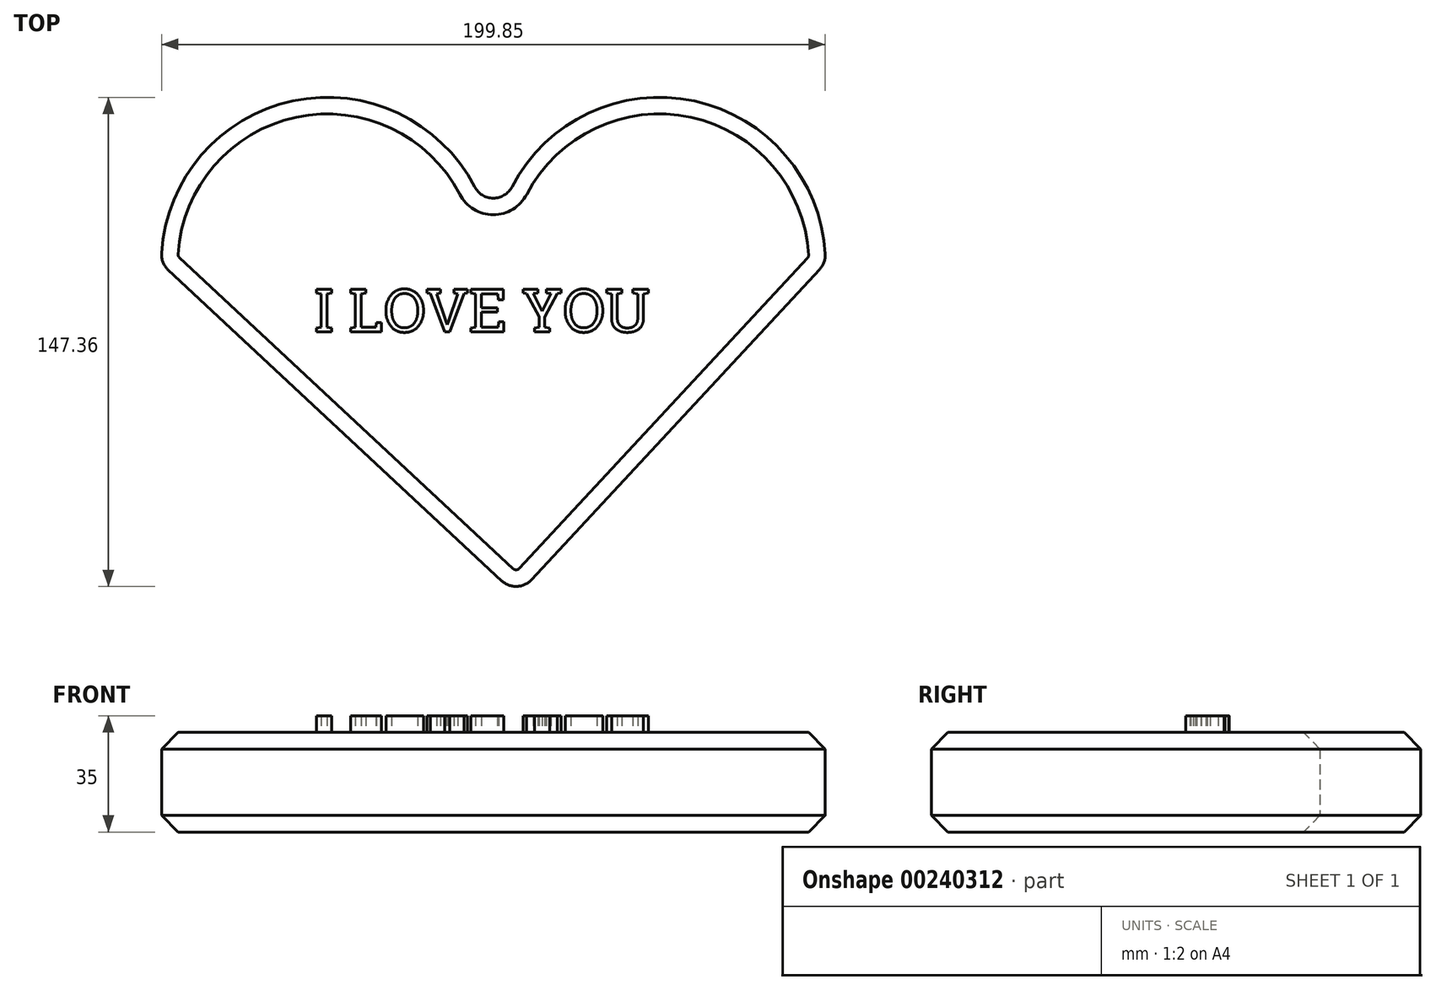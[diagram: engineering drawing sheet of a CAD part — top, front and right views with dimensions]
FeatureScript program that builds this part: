
annotation { "Feature Type Name" : "Feature", "Feature Type Description" : "" }
export const myFeature = defineFeature(function(context is Context, id is Id, definition is map)
    precondition{}
    {
        {
            var Q0;
            Q0=qCreatedBy(makeId("Top.planeOp"),FACE);
            var sketch = newSketch(context, id + "F0", { "sketchPlane" : qUnion([Q0])});
            skLineSegment(sketch, "E0.left", {"start": v(-50, 0) * mm, "end": v(-50, 3.36) * mm, "construction": true});
            skPoint(sketch, "E0.middle", {"position": v(0, 0) * mm});
            skArc(sketch, "E1", {"start": v(-50, 0) * mm, "mid": v(-48.26, 0.03) * mm, "end": v(-46.52, 0.12) * mm});
            skArc(sketch, "E2", {"start": v(50, 0) * mm, "mid": v(51.87, 0.03) * mm, "end": v(53.73, 0.14) * mm});
            skLineSegment(sketch, "E3", {"start": v(2.55, -45.66) * mm, "end": v(-97.9, 48.04) * mm});
            skLineSegment(sketch, "E4", {"start": v(11.54, -45.33) * mm, "end": v(98.24, 48.1) * mm});
            skArc(sketch, "E5.trimOffspring", {"start": v(-5.63, 73.06) * mm, "mid": v(-60.37, 98.91) * mm, "end": v(-99.9, 53.07) * mm});
            skArc(sketch, "E6.trimOffspring", {"start": v(99.92, 52.77) * mm, "mid": v(60.52, 98.88) * mm, "end": v(5.63, 73.06) * mm});
            skPoint(sketch, "E7.orphan", {"position": v(-50, -50) * mm});
            skPoint(sketch, "E8.orphan", {"position": v(50, -50) * mm});
            skPoint(sketch, "E9.visualSharp", {"position": v(0, 50) * mm});
            skArc(sketch, "E9.filletArc", {"start": v(-5.63, 73.06) * mm, "mid": v(0, 69.64) * mm, "end": v(5.63, 73.06) * mm});
            skPoint(sketch, "E10.visualSharp", {"position": v(7.21, -50) * mm});
            skArc(sketch, "E10.filletArc", {"start": v(2.55, -45.66) * mm, "mid": v(7.12, -47.36) * mm, "end": v(11.54, -45.33) * mm});
            skPoint(sketch, "E11.visualSharp", {"position": v(-100, 50) * mm});
            skArc(sketch, "E11.filletArc", {"start": v(-99.9, 53.07) * mm, "mid": v(-99.47, 50.33) * mm, "end": v(-97.9, 48.04) * mm});
            skPoint(sketch, "E12.visualSharp", {"position": v(100, 50) * mm});
            skArc(sketch, "E12.filletArc", {"start": v(98.24, 48.1) * mm, "mid": v(99.56, 50.26) * mm, "end": v(99.92, 52.77) * mm});
            skSolve(sketch);
        }
        {
            var Q0;
            {var subQ6=sQuery(id+"F0.wireOp",EDGE,"E5.trimOffspring");Q0=makeQuery(id+"F0.imprint","IMPRINT",FACE,{"disambiguationData":[TD([[makeQuery(id+"F0.imprint","IMPRINT",EDGE,{"derivedFrom":subQ6}),1.0]])]});}
            extrude(context, id + "F1", {"entities" : qUnion([Q0]), "depth" : 30 * mm});
        }
        {
            var Q0;
            Q0=makeQuery(id+"F1.opExtrude","CAP_FACE",FACE,{"disambiguationData":[OSD([sQuery(id+"F0.wireOp",EDGE,"E3"),sQuery(id+"F0.wireOp",EDGE,"E4"),sQuery(id+"F0.wireOp",EDGE,"E5.trimOffspring"),sQuery(id+"F0.wireOp",EDGE,"E6.trimOffspring"),sQuery(id+"F0.wireOp",EDGE,"E9.filletArc"),sQuery(id+"F0.wireOp",EDGE,"E10.filletArc"),sQuery(id+"F0.wireOp",EDGE,"E11.filletArc"),sQuery(id+"F0.wireOp",EDGE,"E12.filletArc")])],"isStart":false});
            chamfer(context, id + "F2", {"entities" : qUnion([Q0]), "width" : 5 * mm, "tangentPropagation" : true});
        }
        {
            var Q0;
            Q0=makeQuery(id+"F1.opExtrude","CAP_FACE",FACE,{"disambiguationData":[OSD([sQuery(id+"F0.wireOp",EDGE,"E3"),sQuery(id+"F0.wireOp",EDGE,"E4"),sQuery(id+"F0.wireOp",EDGE,"E5.trimOffspring"),sQuery(id+"F0.wireOp",EDGE,"E6.trimOffspring"),sQuery(id+"F0.wireOp",EDGE,"E9.filletArc"),sQuery(id+"F0.wireOp",EDGE,"E10.filletArc"),sQuery(id+"F0.wireOp",EDGE,"E11.filletArc"),sQuery(id+"F0.wireOp",EDGE,"E12.filletArc")])],"isStart":true});
            chamfer(context, id + "F3", {"entities" : qUnion([Q0]), "width" : 5 * mm, "tangentPropagation" : true});
        }
        {
            var Q0;
            Q0=makeQuery(id+"F1.opExtrude","CAP_FACE",FACE,{"disambiguationData":[OSD([sQuery(id+"F0.wireOp",EDGE,"E3"),sQuery(id+"F0.wireOp",EDGE,"E4"),sQuery(id+"F0.wireOp",EDGE,"E5.trimOffspring"),sQuery(id+"F0.wireOp",EDGE,"E6.trimOffspring"),sQuery(id+"F0.wireOp",EDGE,"E9.filletArc"),sQuery(id+"F0.wireOp",EDGE,"E10.filletArc"),sQuery(id+"F0.wireOp",EDGE,"E11.filletArc"),sQuery(id+"F0.wireOp",EDGE,"E12.filletArc")])],"isStart":false});
            var sketch = newSketch(context, id + "F4", { "sketchPlane" : qUnion([Q0])});
            skText(sketch, "E13", { "text": "I LOVE YOU", "fontName": "RobotoSlab-Regular.ttf"});
            const initialGuessF4  = {"E13": [-0.05385, 0.02933, 1, 0, 0.01295]};
            skSetInitialGuess(sketch, initialGuessF4);
            skSolve(sketch);
        }
        {
            var Q0;
            Q0 = qSketchRegion(id + "F4", true);
            extrude(context, id + "F5", {"entities" : qUnion([Q0]), "operationType" : NewBodyOperationType.ADD, "depth" : 5 * mm});
        }
    });
